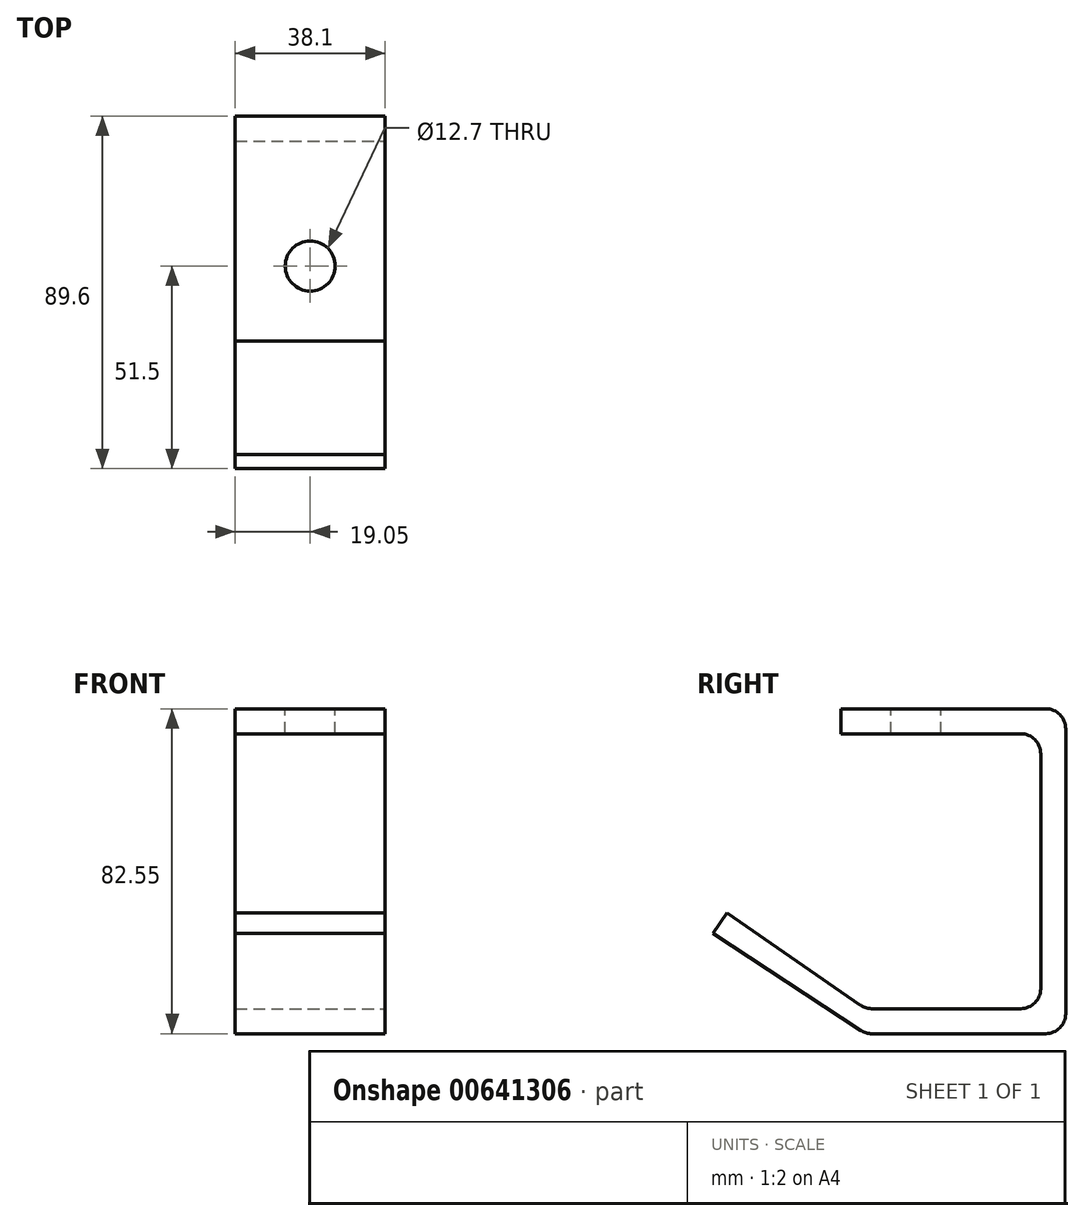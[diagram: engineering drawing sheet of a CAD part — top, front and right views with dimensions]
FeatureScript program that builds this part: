
annotation { "Feature Type Name" : "Feature", "Feature Type Description" : "" }
export const myFeature = defineFeature(function(context is Context, id is Id, definition is map)
    precondition{}
    {
        {
            var Q0;
            Q0=qCreatedBy(makeId("Front.planeOp"),FACE);
            var sketch = newSketch(context, id + "F0", { "sketchPlane" : qUnion([Q0])});
            skLineSegment(sketch, "E0.bottom", {"start": v(-19.05, -41.28) * mm, "end": v(19.05, -41.28) * mm});
            skLineSegment(sketch, "E0.top", {"start": v(-19.05, 41.28) * mm, "end": v(19.05, 41.28) * mm});
            skLineSegment(sketch, "E0.left", {"start": v(-19.05, -41.28) * mm, "end": v(-19.05, 41.28) * mm});
            skLineSegment(sketch, "E0.right", {"start": v(19.05, -41.28) * mm, "end": v(19.05, 41.28) * mm});
            skPoint(sketch, "E0.middle", {"position": v(0, 0) * mm});
            skSolve(sketch);
        }
        {
            var Q0;
            Q0 = qSketchRegion(id + "F0", true);
            extrude(context, id + "F1", {"entities" : qUnion([Q0]), "depth" : 57.15 * mm, "offsetDistance" : 25.4 * mm});
        }
        {
            var Q0;
            Q0=makeQuery(id+"F1.opExtrude","SWEPT_FACE",FACE,{"disambiguationData":[OSD([sQuery(id+"F0.wireOp",EDGE,"E0.right")])]});
            var sketch = newSketch(context, id + "F2", { "sketchPlane" : qUnion([Q0])});
            skLineSegment(sketch, "E1", {"start": v(-57.15, 41.27) * mm, "end": v(-57.15, 34.92) * mm});
            skLineSegment(sketch, "E2", {"start": v(-57.15, 34.92) * mm, "end": v(-6.35, 34.93) * mm});
            skLineSegment(sketch, "E3", {"start": v(-6.35, 34.93) * mm, "end": v(-6.35, -34.93) * mm});
            skLineSegment(sketch, "E4", {"start": v(-6.35, -34.93) * mm, "end": v(-50.8, -34.93) * mm});
            skLineSegment(sketch, "E5", {"start": v(-57.15, 41.27) * mm, "end": v(0, 41.27) * mm});
            skLineSegment(sketch, "E6", {"start": v(0, 41.27) * mm, "end": v(0, -41.28) * mm});
            skLineSegment(sketch, "E7", {"start": v(0, -41.28) * mm, "end": v(-50.8, -41.28) * mm});
            skLineSegment(sketch, "E8", {"start": v(-50.8, -34.93) * mm, "end": v(-50.8, -41.28) * mm});
            skSolve(sketch);
        }
        {
            var Q0;
            {var subQ1=sQuery(id+"F2.wireOp",EDGE,"E2");Q0=makeQuery(id+"F2.imprint","IMPRINT",FACE,{"disambiguationData":[TD([[makeQuery(id+"F2.imprint","IMPRINT",EDGE,{"derivedFrom":subQ1}),-1.0]])]});}
            extrude(context, id + "F3", {"entities" : qUnion([Q0]), "operationType" : NewBodyOperationType.REMOVE, "oppositeDirection" : true, "depth" : 48 * mm, "offsetDistance" : 25.4 * mm});
        }
        {
            var Q0;
            Q0=makeQuery(id+"F1.opExtrude","SWEPT_FACE",FACE,{"disambiguationData":[OSD([sQuery(id+"F0.wireOp",EDGE,"E0.right")])]});
            var sketch = newSketch(context, id + "F4", { "sketchPlane" : qUnion([Q0])});
            skLineSegment(sketch, "E9", {"start": v(-50.8, -34.93) * mm, "end": v(-85.99, -10.6) * mm});
            skLineSegment(sketch, "E10", {"start": v(-85.99, -10.6) * mm, "end": v(-89.6, -15.83) * mm});
            skLineSegment(sketch, "E11", {"start": v(-89.6, -15.83) * mm, "end": v(-50.8, -41.28) * mm});
            skLineSegment(sketch, "E12", {"start": v(-50.8, -34.93) * mm, "end": v(-50.8, -41.28) * mm});
            skLineSegment(sketch, "E13", {"start": v(-50.8, -34.93) * mm, "end": v(-6.35, -34.93) * mm});
            skSolve(sketch);
        }
        {
            var Q0;
            Q0=makeQuery(id+"F4.imprint","IMPRINT",FACE,{"disambiguationData":[TD([[makeQuery(id+"F4.imprint","IMPRINT",EDGE,{"derivedFrom":sQuery(id+"F4.wireOp",EDGE,"E9")}),1.0]])]});
            extrude(context, id + "F5", {"entities" : qUnion([Q0]), "operationType" : NewBodyOperationType.ADD, "oppositeDirection" : true, "depth" : 38.1 * mm, "offsetDistance" : 25.4 * mm});
        }
        {
            var Q0;
            Q0=makeQuery(id+"F1.opExtrude","CAP_EDGE",EDGE,{"disambiguationData":[OSD([sQuery(id+"F0.wireOp",EDGE,"E0.top")])],"isStart":true});
            fillet(context, id + "F6", {"entities" : qUnion([Q0]), "radius" : 5.08 * mm, "tangentPropagation" : true, "allowEdgeOverflow" : false});
        }
        {
            var Q0;
            Q0=makeQuery(id+"F3.boolean.opBoolean","COPY",EDGE,{"derivedFrom":makeQuery(id+"F3.opExtrude","SWEPT_EDGE",EDGE,{"disambiguationData":[OSD([sQuery(id+"F2.wireOp",EDGE,"E2"),sQuery(id+"F2.wireOp",EDGE,"E3")])]})});
            fillet(context, id + "F7", {"entities" : qUnion([Q0]), "radius" : 5.08 * mm, "tangentPropagation" : true, "allowEdgeOverflow" : false});
        }
        {
            var Q0;
            Q0=makeQuery(id+"F1.opExtrude","CAP_EDGE",EDGE,{"disambiguationData":[OSD([sQuery(id+"F0.wireOp",EDGE,"E0.bottom")])],"isStart":true});
            fillet(context, id + "F8", {"entities" : qUnion([Q0]), "radius" : 5.08 * mm, "tangentPropagation" : true, "allowEdgeOverflow" : false});
        }
        {
            var Q0;
            Q0=makeQuery(id+"F3.boolean.opBoolean","COPY",EDGE,{"derivedFrom":makeQuery(id+"F3.opExtrude","SWEPT_EDGE",EDGE,{"disambiguationData":[OSD([sQuery(id+"F2.wireOp",EDGE,"E3"),sQuery(id+"F2.wireOp",EDGE,"E4")])]})});
            fillet(context, id + "F9", {"entities" : qUnion([Q0]), "radius" : 5.08 * mm, "tangentPropagation" : true, "allowEdgeOverflow" : false});
        }
        {
            var Q0;
            {var subQ0=sQuery(id+"F2.wireOp",EDGE,"E4");Q0=makeQuery(id+"F5.boolean.opBoolean","MERGE",EDGE,{"derivedFrom":[makeQuery(id+"F3.boolean.opBoolean","COPY",EDGE,{"derivedFrom":makeQuery(id+"F3.opExtrude","SWEPT_EDGE",EDGE,{"disambiguationData":[OSD([subQ0,sQuery(id+"F2.wireOp",EDGE,"E8")])]})}),makeQuery(id+"F5.opExtrude","SWEPT_EDGE",EDGE,{"disambiguationData":[OSD([subQ0,sQuery(id+"F4.wireOp",EDGE,"E9"),sQuery(id+"F4.wireOp",EDGE,"E12")])]})]});}
            var Q1;
            {var subQ0=sQuery(id+"F0.wireOp",EDGE,"E0.right");var subQ1=sQuery(id+"F0.wireOp",EDGE,"E0.bottom");Q1=makeQuery(id+"F5.boolean.opBoolean","MERGE",EDGE,{"derivedFrom":[makeQuery(id+"F3.boolean.opBoolean","COPY",EDGE,{"derivedFrom":makeQuery(id+"F3.opExtrude","SWEPT_EDGE",EDGE,{"disambiguationData":[OSD([subQ1,subQ0,sQuery(id+"F2.wireOp",EDGE,"E7"),sQuery(id+"F2.wireOp",EDGE,"E8")])]})}),makeQuery(id+"F5.opExtrude","SWEPT_EDGE",EDGE,{"disambiguationData":[OSD([subQ1,subQ0,sQuery(id+"F4.wireOp",EDGE,"E11"),sQuery(id+"F4.wireOp",EDGE,"E12")])]})]});}
            fillet(context, id + "F10", {"entities" : qUnion([Q0, Q1]), "radius" : 5.08 * mm, "tangentPropagation" : true, "allowEdgeOverflow" : false});
        }
        {
            var Q0;
            Q0=makeQuery(id+"F1.opExtrude","SWEPT_FACE",FACE,{"disambiguationData":[OSD([sQuery(id+"F0.wireOp",EDGE,"E0.top")])]});
            var sketch = newSketch(context, id + "F11", { "sketchPlane" : qUnion([Q0])});
            skCircle(sketch, "E14", {"center": v(0, -38.1) * mm, "radius": 6.35 * mm});
            skSolve(sketch);
        }
        {
            var Q0;
            Q0 = qSketchRegion(id + "F11", true);
            extrude(context, id + "F12", {"entities" : qUnion([Q0]), "operationType" : NewBodyOperationType.REMOVE, "oppositeDirection" : true, "depth" : 25.4 * mm, "offsetDistance" : 25.4 * mm});
        }
    });
